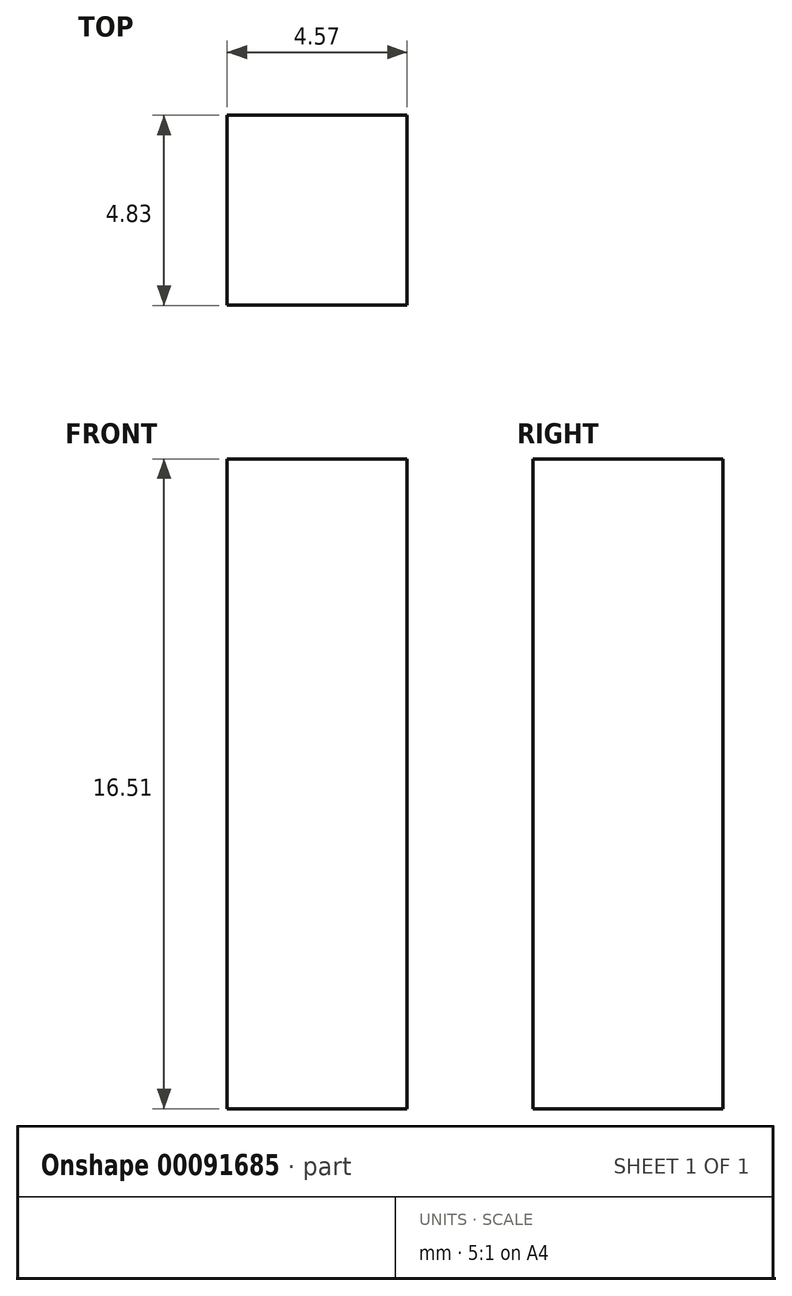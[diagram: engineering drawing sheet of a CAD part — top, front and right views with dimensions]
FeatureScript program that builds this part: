
annotation { "Feature Type Name" : "Feature", "Feature Type Description" : "" }
export const myFeature = defineFeature(function(context is Context, id is Id, definition is map)
    precondition{}
    {
        {
            var Q0;
            Q0=qCreatedBy(makeId("Top.planeOp"),FACE);
            var sketch = newSketch(context, id + "F0", { "sketchPlane" : qUnion([Q0])});
            skLineSegment(sketch, "E0.bottom", {"start": v(-34.67, 15.37) * mm, "end": v(-30.1, 15.37) * mm});
            skLineSegment(sketch, "E0.top", {"start": v(-34.67, 10.54) * mm, "end": v(-30.1, 10.54) * mm});
            skLineSegment(sketch, "E0.left", {"start": v(-34.67, 15.37) * mm, "end": v(-34.67, 10.54) * mm});
            skLineSegment(sketch, "E0.right", {"start": v(-30.1, 15.37) * mm, "end": v(-30.1, 10.54) * mm});
            skSolve(sketch);
        }
        {
            var Q0;
            Q0=makeQuery(id+"F0.imprint","IMPRINT",FACE,{"disambiguationData":[TD([[makeQuery(id+"F0.imprint","IMPRINT",EDGE,{"derivedFrom":sQuery(id+"F0.wireOp",EDGE,"E0.bottom")}),-1.0]])]});
            extrude(context, id + "F1", {"entities" : qUnion([Q0]), "depth" : 16.5 * mm});
        }
    });
